# Revit family: Fire-Smoke-Curtain_Manual_DoorSystems_DSI-M10D
name_source: partatom
category: Doors
units: mm (PartAtom-declared; Revit-internal decimal feet)

## family parameters
Always vertical = Yes
Cut with Voids When Loaded = No
Host = Wall
OmniClass Number = 23.30.10.21.11.11
OmniClass Title = Rolling Fire Doors
Room Calculation Point = No
Shared = No

## types (1)
- Single Roller
    Analytic Construction = <None>
    CAD Details = https://www.arcat.com
    CurtainDrop_Viz = Yes
    Define Thermal Properties by = Schematic Type
    Description = Manual Fire Protective Smoke Curtain
    Fire Performance = UL 10D 1 HR
    Frame Depth = 0' - 2"
    Frame Width = 0' - 4"
    Keynote = 07 87 70
    Manufacturer = Door Systems
    Model = DSI-M10D
    Product Page URL = https://www.arcat.com
    Rough Height = 0' - 0"
    Rough Width = 0' - 0"
    Specification = https://www.arcat.com
    Standards Conformance = ICC  ;  UL 1784 S Label  ;  UL 864  ;  OSHPD  ;  LAFD High Rise
    Thickness = 0' - 0"
    URL = https://www.doorsysinc.com
    Wall Closure = By host

## geometry (parser evidence)
native form markers: Sweep x2
no freeform markers — native parametric forms only
